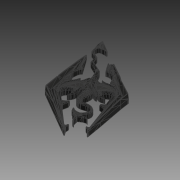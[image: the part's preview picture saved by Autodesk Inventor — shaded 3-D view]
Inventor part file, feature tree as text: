
AUTODESK INVENTOR PART (.ipt)
format: ipt  version: 2018 (Build 220112000, 112)  size: 5,841,920 bytes
history: native  units: mm
features: other x4, extrude x1, sketch x1
ambient origin geometry x8: Origin, YZ Plane, XZ Plane, XY Plane, X Axis, Y Axis, Z Axis, Center Point
bodies: Body1 (feature_tree)
feature tree (6):
  other  "skyrimlogo2.ipt"
  extrude  "押し出し1"  Depth=0.769231mm
  other  "ソリッド1::skyrimlogo2.ipt"
  other  "TaggingFeature1"
  sketch  "スケッチ1"
  other  "ソリッド1"
